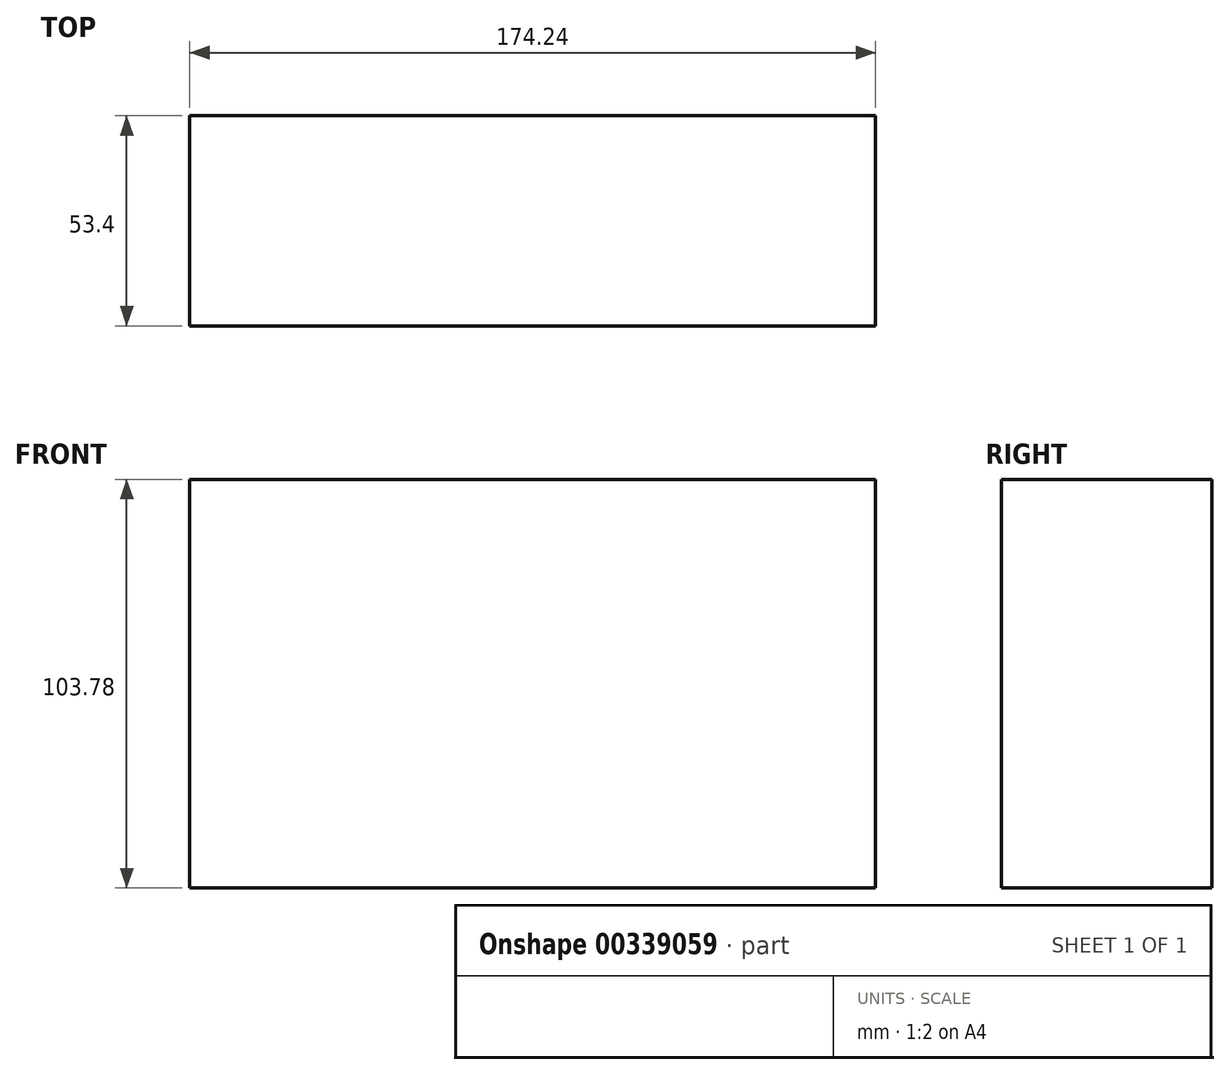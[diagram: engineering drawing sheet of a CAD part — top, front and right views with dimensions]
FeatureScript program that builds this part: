
annotation { "Feature Type Name" : "Feature", "Feature Type Description" : "" }
export const myFeature = defineFeature(function(context is Context, id is Id, definition is map)
    precondition{}
    {
        {
            var Q0;
            Q0=qCreatedBy(makeId("Right.planeOp"),FACE);
            var sketch = newSketch(context, id + "F0", { "sketchPlane" : qUnion([Q0])});
            skLineSegment(sketch, "E0.bottom", {"start": v(26.7, -51.9) * mm, "end": v(-26.7, -51.9) * mm});
            skLineSegment(sketch, "E0.top", {"start": v(26.7, 51.9) * mm, "end": v(-26.7, 51.9) * mm});
            skLineSegment(sketch, "E0.left", {"start": v(26.7, -51.9) * mm, "end": v(26.7, 51.9) * mm});
            skLineSegment(sketch, "E0.right", {"start": v(-26.7, -51.9) * mm, "end": v(-26.7, 51.9) * mm});
            skPoint(sketch, "E0.middle", {"position": v(0, 0) * mm});
            skSolve(sketch);
        }
        {
            var Q0;
            Q0 = qSketchRegion(id + "F0", true);
            extrude(context, id + "F1", {"entities" : qUnion([Q0]), "depth" : 174.24 * mm});
        }
    });
